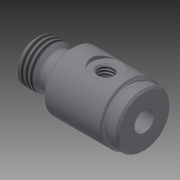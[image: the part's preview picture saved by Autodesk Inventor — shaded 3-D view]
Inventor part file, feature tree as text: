
AUTODESK INVENTOR PART (.ipt)
format: ipt  version: 2014 (Build 180170000, 170)  size: 240,128 bytes
history: native  units: in
note: dims shown in document units (in); Inventor stores cm internally (conversion verified against a paired STEP export)
features: other x84, sketch x5, revolve x4, thread x2, hole x1
ambient origin geometry x8: Origin, YZ Plane, XZ Plane, XY Plane, X Axis, Y Axis, Z Axis, Center Point
bodies: Solid1 (feature_tree)
feature tree (96):
  revolve  "Revolution1"  [1 undecoded]
  thread  "Thread1"  [1 undecoded]
  revolve  "Revolution2"  Angle=360.0deg
  hole  "Hole1"  [1 undecoded]
  revolve  "Revolution3"  [1 undecoded]
  thread  "Thread2"  [1 undecoded]
  revolve  "Revolution4"  [1 undecoded]
  other  "c2_XY"
  other  "c2_YZ"
  other  "c2_ZX"
  other  "c2_X"
  other  "c2_Y"
  other  "c2_Z"
  other  "c2_Center"
  other  "e2_XY"
  other  "e2_YZ"
  other  "e2_ZX"
  other  "e2_X"
  other  "e2_Y"
  other  "e2_Z"
  other  "e2_Center"
  other  "f1_XY"
  other  "f1_YZ"
  other  "f1_ZX"
  other  "f1_X"
  other  "f1_Y"
  other  "f1_Z"
  other  "f1_Center"
  other  "f2_XY"
  other  "f2_YZ"
  other  "f2_ZX"
  other  "f2_X"
  other  "f2_Y"
  other  "f2_Z"
  other  "f2_Center"
  other  "i1_XY"
  other  "i1_YZ"
  other  "i1_ZX"
  other  "i1_X"
  other  "i1_Y"
  other  "i1_Z"
  other  "i1_Center"
  other  "i2_XY"
  other  "i2_YZ"
  other  "i2_ZX"
  other  "i2_X"
  other  "i2_Y"
  other  "i2_Z"
  other  "i2_Center"
  other  "l1_XY"
  other  "l1_YZ"
  other  "l1_ZX"
  other  "l1_X"
  other  "l1_Y"
  other  "l1_Z"
  other  "l1_Center"
  other  "l2_XY"
  other  "l2_YZ"
  other  "l2_ZX"
  other  "l2_X"
  other  "l2_Y"
  other  "l2_Z"
  other  "l2_Center"
  other  "rod_guide_XY"
  other  "rod_guide_YZ"
  other  "rod_guide_ZX"
  other  "rod_guide_X"
  other  "rod_guide_Y"
  other  "rod_guide_Z"
  other  "rod_guide_Center"
  other  "to_mounting_bracket_XY"
  other  "to_mounting_bracket_YZ"
  other  "to_mounting_bracket_ZX"
  other  "to_mounting_bracket_X"
  other  "to_mounting_bracket_Y"
  other  "to_mounting_bracket_Z"
  other  "to_mounting_bracket_Center"
  other  "to_rod_XY"
  other  "to_rod_YZ"
  other  "to_rod_ZX"
  other  "to_rod_X"
  other  "to_rod_Y"
  other  "to_rod_Z"
  other  "to_rod_Center"
  other  "to_tube_XY"
  other  "to_tube_YZ"
  other  "to_tube_ZX"
  other  "to_tube_X"
  other  "to_tube_Y"
  other  "to_tube_Z"
  other  "to_tube_Center"
  sketch  "Sketch_2"  dims[d0=360.0deg d1=0.1557in d2=0.0in d3=360.0deg]
  sketch  "Sketch_3"  dims[d4=0.21in d5=0.75in d6=0.25in d7=0.25in d8=90.0deg d9=1.156in d10=0.0in d11=360.0deg]
  sketch  "Sketch3"  dims[d12=0.0955in d13=0.1018in d14=360.0deg]
  sketch  "Sketch_13"
  sketch  "Sketch_47"
note: 6 required parameter values undecoded (feature->parameter linkage not recoverable at this tier; creation-order binding heuristic only, values carry confidence <= 0.55)